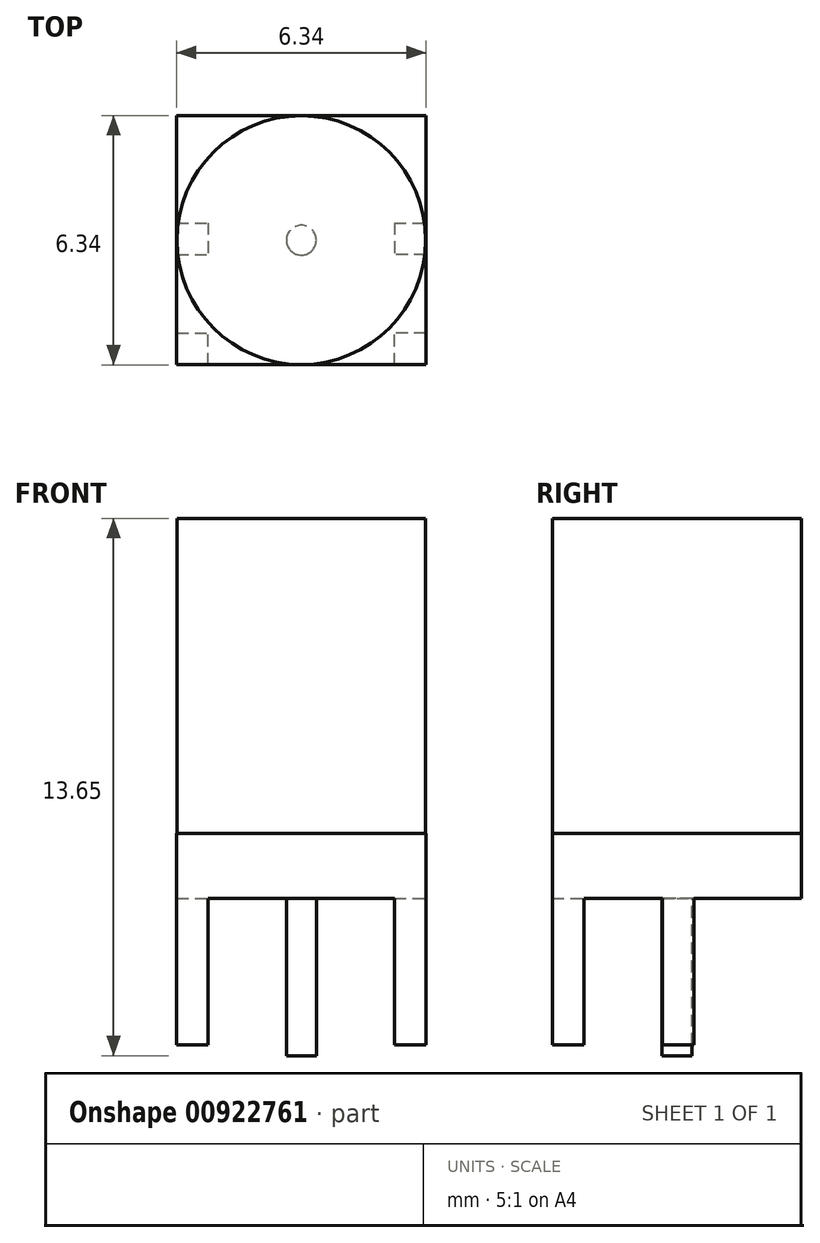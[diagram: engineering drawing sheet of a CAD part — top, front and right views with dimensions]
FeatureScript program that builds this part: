
annotation { "Feature Type Name" : "Feature", "Feature Type Description" : "" }
export const myFeature = defineFeature(function(context is Context, id is Id, definition is map)
    precondition{}
    {
        {
            var Q0;
            Q0=qCreatedBy(makeId("Top.planeOp"),FACE);
            var sketch = newSketch(context, id + "F0", { "sketchPlane" : qUnion([Q0])});
            skLineSegment(sketch, "E0.bottom", {"start": v(-3.17, 3.17) * mm, "end": v(3.17, 3.17) * mm});
            skLineSegment(sketch, "E0.top", {"start": v(-3.17, -3.17) * mm, "end": v(3.17, -3.17) * mm});
            skLineSegment(sketch, "E0.left", {"start": v(-3.17, 3.17) * mm, "end": v(-3.17, -3.17) * mm});
            skLineSegment(sketch, "E0.right", {"start": v(3.17, 3.17) * mm, "end": v(3.17, -3.17) * mm});
            skSolve(sketch);
        }
        {
            var Q0;
            Q0 = qSketchRegion(id + "F0", true);
            extrude(context, id + "F1", {"entities" : qUnion([Q0]), "depth" : 1.65 * mm, "offsetDistance" : 25 * mm});
        }
        {
            var Q0;
            Q0=makeQuery(id+"F1.opExtrude","CAP_FACE",FACE,{"disambiguationData":[OSD([sQuery(id+"F0.wireOp",EDGE,"E0.bottom"),sQuery(id+"F0.wireOp",EDGE,"E0.top"),sQuery(id+"F0.wireOp",EDGE,"E0.left"),sQuery(id+"F0.wireOp",EDGE,"E0.right")])],"isStart":true});
            var sketch = newSketch(context, id + "F2", { "sketchPlane" : qUnion([Q0])});
            skLineSegment(sketch, "E1.bottom", {"start": v(-3.17, 3.17) * mm, "end": v(-2.37, 3.17) * mm});
            skLineSegment(sketch, "E1.top", {"start": v(-3.17, 2.37) * mm, "end": v(-2.37, 2.37) * mm});
            skLineSegment(sketch, "E1.left", {"start": v(-3.17, 3.17) * mm, "end": v(-3.17, 2.37) * mm});
            skLineSegment(sketch, "E1.right", {"start": v(-2.37, 3.17) * mm, "end": v(-2.37, 2.37) * mm});
            skLineSegment(sketch, "E2.bottom", {"start": v(3.17, 3.17) * mm, "end": v(2.37, 3.17) * mm});
            skLineSegment(sketch, "E2.top", {"start": v(3.17, 2.37) * mm, "end": v(2.37, 2.37) * mm});
            skLineSegment(sketch, "E2.left", {"start": v(3.17, 3.17) * mm, "end": v(3.17, 2.37) * mm});
            skLineSegment(sketch, "E2.right", {"start": v(2.37, 3.17) * mm, "end": v(2.37, 2.37) * mm});
            skLineSegment(sketch, "E3.bottom", {"start": v(-3.17, -0.43) * mm, "end": v(-2.36, -0.43) * mm});
            skLineSegment(sketch, "E3.top", {"start": v(-3.17, 0.37) * mm, "end": v(-2.37, 0.37) * mm});
            skLineSegment(sketch, "E3.right", {"start": v(-2.36, -0.43) * mm, "end": v(-2.37, 0.37) * mm});
            skLineSegment(sketch, "E4.top", {"start": v(3.17, 0.37) * mm, "end": v(2.37, 0.37) * mm});
            skLineSegment(sketch, "E4.left", {"start": v(3.17, -0.43) * mm, "end": v(3.17, 0.37) * mm});
            skLineSegment(sketch, "E4.right", {"start": v(2.37, -0.43) * mm, "end": v(2.37, 0.37) * mm});
            skLineSegment(sketch, "E5", {"start": v(2.37, -0.43) * mm, "end": v(3.17, -0.43) * mm});
            skLineSegment(sketch, "E6", {"start": v(-3.17, 0.37) * mm, "end": v(-3.17, -0.43) * mm});
            skSolve(sketch);
        }
        {
            var Q0;
            Q0=makeQuery(id+"F2.imprint","IMPRINT",FACE,{"disambiguationData":[TD([[makeQuery(id+"F2.imprint","IMPRINT",EDGE,{"derivedFrom":sQuery(id+"F2.wireOp",EDGE,"E1.bottom")}),-1.0]])]});
            var Q1;
            Q1=makeQuery(id+"F2.imprint","IMPRINT",FACE,{"disambiguationData":[TD([[makeQuery(id+"F2.imprint","IMPRINT",EDGE,{"derivedFrom":sQuery(id+"F2.wireOp",EDGE,"E3.bottom")}),1.0]])]});
            var Q2;
            Q2=makeQuery(id+"F2.imprint","IMPRINT",FACE,{"disambiguationData":[TD([[makeQuery(id+"F2.imprint","IMPRINT",EDGE,{"derivedFrom":sQuery(id+"F2.wireOp",EDGE,"E4.top")}),1.0]])]});
            var Q3;
            Q3=makeQuery(id+"F2.imprint","IMPRINT",FACE,{"disambiguationData":[TD([[makeQuery(id+"F2.imprint","IMPRINT",EDGE,{"derivedFrom":sQuery(id+"F2.wireOp",EDGE,"E2.bottom")}),-1.0]])]});
            extrude(context, id + "F3", {"entities" : qUnion([Q0, Q1, Q2, Q3]), "operationType" : NewBodyOperationType.ADD, "depth" : 3.72 * mm, "offsetDistance" : 25 * mm});
        }
        {
            var Q0;
            Q0=makeQuery(id+"F1.opExtrude","CAP_FACE",FACE,{"disambiguationData":[OSD([sQuery(id+"F0.wireOp",EDGE,"E0.bottom"),sQuery(id+"F0.wireOp",EDGE,"E0.top"),sQuery(id+"F0.wireOp",EDGE,"E0.left"),sQuery(id+"F0.wireOp",EDGE,"E0.right")])],"isStart":false});
            var sketch = newSketch(context, id + "F4", { "sketchPlane" : qUnion([Q0])});
            skCircle(sketch, "E7", {"center": v(0, 0) * mm, "radius": 3.16 * mm});
            skSolve(sketch);
        }
        {
            var Q0;
            Q0 = qSketchRegion(id + "F4", true);
            extrude(context, id + "F5", {"entities" : qUnion([Q0]), "operationType" : NewBodyOperationType.ADD, "depth" : 8 * mm, "offsetDistance" : 25 * mm});
        }
        {
            var Q0;
            Q0=makeQuery(id+"F1.opExtrude","CAP_FACE",FACE,{"disambiguationData":[OSD([sQuery(id+"F0.wireOp",EDGE,"E0.bottom"),sQuery(id+"F0.wireOp",EDGE,"E0.top"),sQuery(id+"F0.wireOp",EDGE,"E0.left"),sQuery(id+"F0.wireOp",EDGE,"E0.right")])],"isStart":true});
            var sketch = newSketch(context, id + "F6", { "sketchPlane" : qUnion([Q0])});
            skCircle(sketch, "E8", {"center": v(0, 0) * mm, "radius": 0.38 * mm});
            skSolve(sketch);
        }
        {
            var Q0;
            Q0 = qSketchRegion(id + "F6", true);
            extrude(context, id + "F7", {"entities" : qUnion([Q0]), "operationType" : NewBodyOperationType.ADD, "depth" : 4 * mm, "offsetDistance" : 25 * mm});
        }
    });
